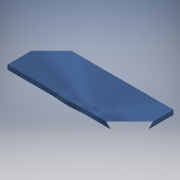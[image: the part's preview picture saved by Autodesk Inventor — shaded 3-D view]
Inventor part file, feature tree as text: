
AUTODESK INVENTOR PART (.ipt)
format: ipt  version: 2016 (Build 200138000, 138)  size: 102,400 bytes
history: native  units: mm
features: reference x2, extrude x1, sketch x1
ambient origin geometry x8: Origin, YZ Plane, XZ Plane, XY Plane, X Axis, Y Axis, Z Axis, Center Point
bodies: Solid1 (feature_tree)
feature tree (4):
  extrude  "Extrusion1"  [1 undecoded]
  sketch  "Sketch1"  dims[d0=3.0mm d1=0.0mm]
  reference  "Reference3"
  reference  "Reference4"
note: 1 required parameter value undecoded (feature->parameter linkage not recoverable at this tier; creation-order binding heuristic only, values carry confidence <= 0.55)
